# Revit family: Door-Industrial_Door-Dynaco-M2_Compact
name_source: partatom
category: Doors
revit_build: Autodesk Revit 2016 (Build: 20150714_1515(x64)
units: mm (PartAtom-declared; Revit-internal decimal feet)

## family parameters
Always vertical = Yes
Cut with Voids When Loaded = No
Host = Wall
Room Calculation Point = No
Shared = No

## types (2) — shared parameters
Air permeability, EN 12426 = class 1 (24 m3/m2/ h at 50 Pa)
/m2
/h at 50 Pa)
Analytic Construction = <None>
BIMobject category = Industrial Doors
C1 = Yes
C2 = Yes
C3 = Yes
C4 = Yes
C5 = Yes
Closing Speed = 1,2 m/s
Control Unit Distance = 600 mm
Control unit Height = 1500 mm  [stored 4.92126 ft]
Date of publishing = 2015-10-01
Depth = 0.00
Design country = Belgium
Edition number = 1
Five Column Windows = Yes
Five Row Windows = Yes
Four Column Windows = No
Four Row Windows = No
IFC Classification = Door
Lifetime expectations = 1.000.000 cycles
Manufacturer country = Belgium
Manufacturer name = Entrematic
Material main = PVC
Material secondary = Steel
NBS Reference Code = 59-23-38
NBS Reference Description = High Speed Doorsets
Nominal height = 550000
Nominal width = 550000
One Column Windows = No
One Row Windows = No
Opening Speed = up to 2,4 m/s 2
Option 1 = Stainless steel
Product Guid = e93b2853-f502-4f8c-b12e-6ccf43d4ce35
Product SKU = dyn-m2-com
Product data url = https://bimobject.com
Product family = High speed door
Product group = Inside door
QR code = http://bimobject.com
R1 = Yes
R2 = Yes
R3 = Yes
R4 = Yes
R5 = Yes
Reduced Lintel = Yes
Technical description = https://www.dynacodoor.com
Thermal transmittance = 6,02 W/ (m2 K)
K)
Three Column Windows = No
Three Row Windows = No
Two Column Windows = No
Two Row Windows = No
UNSPSC Code = 301715
Uniclass 1.4 Code = L411
Uniclass 1.4 Description = Doors
Uniclass 2.0 Code = PR-59-23-38
Uniclass 2.0 Description = High Speed Doorsets
Water penetration, EN 12425 = class 1 (30 N/m2)
)
Wind load resistance, EN 12424 = class 1 (300 N/m2)
)
zero-valued in all types: Weight Net (Kg)

## per-type parameters (varying)
| type | Vision Panel |
| Dynaco_M2_Compact_400 | 400 |
| Dynaco_M2_Compact_800 | 800 |

note: [stored X ft] marks values corroborated as IEEE doubles in the binary element streams (Revit-internal decimal feet)

## geometry (parser evidence)
native form markers: Blend x6, Sweep x20
no freeform markers — native parametric forms only
